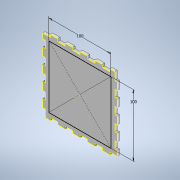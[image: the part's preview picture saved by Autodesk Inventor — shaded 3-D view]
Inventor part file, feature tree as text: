
AUTODESK INVENTOR PART (.ipt)
format: ipt  version: 2021 (Build 250183000, 183)  size: 376,320 bytes
history: native  units: mm
features: sketch x5, extrude x4, pattern_linear x2, pattern_circular x2, projected_geometry x2, other x1
ambient origin geometry x8: Origin, YZ Plane, XZ Plane, XY Plane, X Axis, Y Axis, Z Axis, Center Point
bodies: Solid1 (feature_tree)
feature tree (16):
  extrude  "Extrusion1"  Depth=120.0mm
  extrude  "Extrusion2"  Depth=60.0mm
  pattern_linear  "side_top"  Spacing1=12.0mm  [1 undecoded]
  extrude  "Extrusion3"  Depth=4.0mm
  pattern_circular  "side_bottom"  [2 undecoded]
  pattern_linear  "side_left"  Count1=5  [1 undecoded]
  pattern_circular  "side_right"  [2 undecoded]
  extrude  "Extrusion5"  Depth=4.0mm TaperAngle=0.0deg
  sketch  "Sketch7"  dims[d17=0.0mm d18=12.0mm d19=4.0mm d20=0.0mm d21=50.0mm d23=24.0mm d24=10.0mm d26=0.0mm d28=4.0mm d29=0.0mm d46=20.0mm d47=360.0deg d49=4.0mm d50=12.0mm d51=0.0mm d52=0.0mm d53=50.0mm d55=24.0mm d56=20.0mm d57=360.0deg d59=0.11mm d60=4.0mm d61=0.0mm d62=100.0mm d63=100.0mm]
  sketch  "Sketch1"  dims[d0=120.0mm d1=120.0mm]
  sketch  "Sketch3"  dims[d2=60.0mm d3=60.0mm]
  sketch  "Sketch4"  dims[d4=4.0mm]
  other  "Work Axis2"
  sketch  "Sketch6"  dims[d5=0.0mm]
  projected_geometry  "Projected Loop1"
  projected_geometry  "Projected Loop2"
note: 6 required parameter values undecoded (feature->parameter linkage not recoverable at this tier; creation-order binding heuristic only, values carry confidence <= 0.55)
